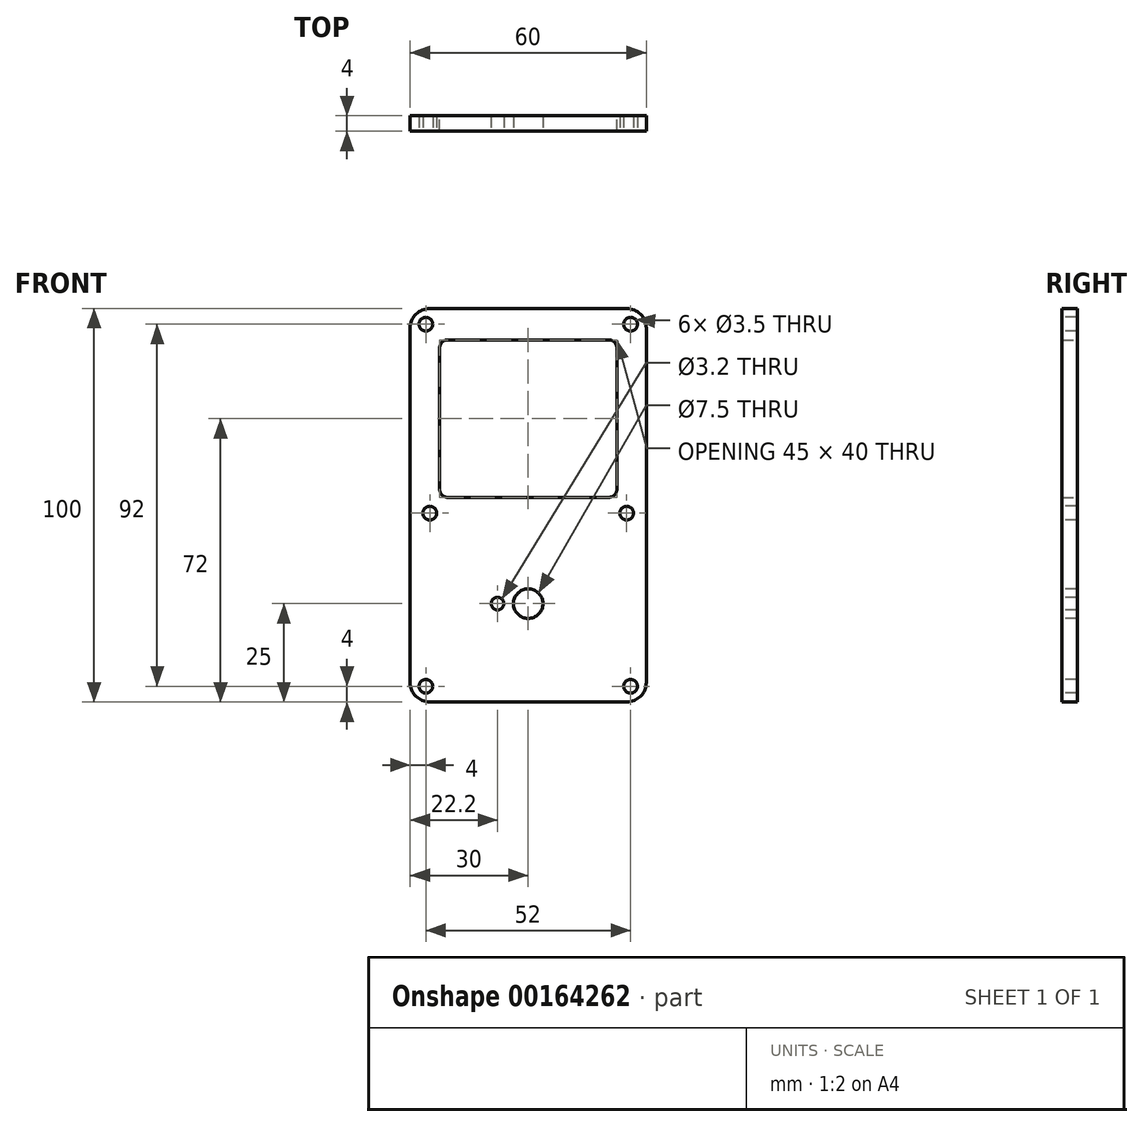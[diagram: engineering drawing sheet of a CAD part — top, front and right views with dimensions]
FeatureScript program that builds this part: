
annotation { "Feature Type Name" : "Feature", "Feature Type Description" : "" }
export const myFeature = defineFeature(function(context is Context, id is Id, definition is map)
    precondition{}
    {
        {
            var Q0;
            Q0=qCreatedBy(makeId("Front.planeOp"),FACE);
            var sketch = newSketch(context, id + "F0", { "sketchPlane" : qUnion([Q0])});
            skLineSegment(sketch, "E0.bottom", {"start": v(-30, 50) * mm, "end": v(30, 50) * mm});
            skLineSegment(sketch, "E0.top", {"start": v(-30, -50) * mm, "end": v(30, -50) * mm});
            skLineSegment(sketch, "E0.left", {"start": v(-30, 50) * mm, "end": v(-30, -50) * mm});
            skLineSegment(sketch, "E0.right", {"start": v(30, 50) * mm, "end": v(30, -50) * mm});
            skPoint(sketch, "E0.middle", {"position": v(0, 0) * mm});
            skLineSegment(sketch, "E1.bottom", {"start": v(-22.5, 42) * mm, "end": v(22.5, 42) * mm});
            skLineSegment(sketch, "E1.top", {"start": v(-22.5, 2) * mm, "end": v(22.5, 2) * mm});
            skLineSegment(sketch, "E1.left", {"start": v(-22.5, 42) * mm, "end": v(-22.5, 2) * mm});
            skLineSegment(sketch, "E1.right", {"start": v(22.5, 42) * mm, "end": v(22.5, 2) * mm});
            skSolve(sketch);
        }
        {
            var Q0;
            Q0 = qSketchRegion(id + "F0", true);
            extrude(context, id + "F1", {"entities" : qUnion([Q0]), "depth" : 4 * mm});
        }
        {
            var Q0;
            Q0=makeQuery(id+"F1.opExtrude","CAP_FACE",FACE,{"disambiguationData":[OSD([sQuery(id+"F0.wireOp",EDGE,"E0.bottom"),sQuery(id+"F0.wireOp",EDGE,"E0.top"),sQuery(id+"F0.wireOp",EDGE,"E0.left"),sQuery(id+"F0.wireOp",EDGE,"E0.right"),sQuery(id+"F0.wireOp",EDGE,"E1.bottom"),sQuery(id+"F0.wireOp",EDGE,"E1.top"),sQuery(id+"F0.wireOp",EDGE,"E1.left"),sQuery(id+"F0.wireOp",EDGE,"E1.right")])],"isStart":false});
            var sketch = newSketch(context, id + "F2", { "sketchPlane" : qUnion([Q0])});
            skLineSegment(sketch, "E2.bottom", {"start": v(-26, 46) * mm, "end": v(26, 46) * mm});
            skLineSegment(sketch, "E2.top", {"start": v(-26, -46) * mm, "end": v(26, -46) * mm});
            skLineSegment(sketch, "E2.left", {"start": v(-26, 46) * mm, "end": v(-26, -46) * mm});
            skLineSegment(sketch, "E2.right", {"start": v(26, 46) * mm, "end": v(26, -46) * mm});
            skPoint(sketch, "E2.middle", {"position": v(0, 0) * mm});
            skPoint(sketch, "E3", {"position": v(0, -25) * mm});
            skSolve(sketch);
        }
        {
            var Q0;
            Q0=sQuery(id+"F2.wireOp",VERTEX,"E2.left.start");
            var Q1;
            Q1=sQuery(id+"F2.wireOp",VERTEX,"E2.right.start");
            var Q2;
            Q2=sQuery(id+"F2.wireOp",VERTEX,"c73e0ecb-fc85-44dc-a880-6b6466e35b10");
            var Q3;
            Q3=sQuery(id+"F2.wireOp",VERTEX,"E2.top.end");
            var Q4;
            Q4=sQuery(id+"F2.wireOp",VERTEX,"E2.left.end");
            var Q5;
            Q5=sQuery(id+"F2.wireOp",VERTEX,"a1096d60-7892-4570-80c7-3819a983ac6c");
            var Q6;
            Q6=makeQuery(id+"F1.opExtrude","SWEPT_BODY",BODY,{"disambiguationData":[OSD([sQuery(id+"F0.wireOp",EDGE,"E0.bottom"),sQuery(id+"F0.wireOp",EDGE,"E0.top"),sQuery(id+"F0.wireOp",EDGE,"E0.left"),sQuery(id+"F0.wireOp",EDGE,"E0.right"),sQuery(id+"F0.wireOp",EDGE,"E1.bottom"),sQuery(id+"F0.wireOp",EDGE,"E1.top"),sQuery(id+"F0.wireOp",EDGE,"E1.left"),sQuery(id+"F0.wireOp",EDGE,"E1.right")])]});
            hole(context, id + "F3", {"style" : HoleStyle.SIMPLE, "endStyle" : HoleEndStyle.BLIND, "holeDiameter" : 3.5 * mm, "holeDepth" : 25 * mm, "startFromSketch" : true, "locations" : qUnion([Q0, Q1, Q2, Q3, Q4, Q5]), "scope" : qUnion([Q6])});
        }
        {
            var Q0;
            Q0=makeQuery(id+"F1.opExtrude","CAP_FACE",FACE,{"disambiguationData":[OSD([sQuery(id+"F0.wireOp",EDGE,"E0.bottom"),sQuery(id+"F0.wireOp",EDGE,"E0.top"),sQuery(id+"F0.wireOp",EDGE,"E0.left"),sQuery(id+"F0.wireOp",EDGE,"E0.right"),sQuery(id+"F0.wireOp",EDGE,"E1.bottom"),sQuery(id+"F0.wireOp",EDGE,"E1.top"),sQuery(id+"F0.wireOp",EDGE,"E1.left"),sQuery(id+"F0.wireOp",EDGE,"E1.right")])],"isStart":false});
            var sketch = newSketch(context, id + "F4", { "sketchPlane" : qUnion([Q0])});
            skPoint(sketch, "E4", {"position": v(0, -25) * mm});
            skCircle(sketch, "E5", {"center": v(0, -25) * mm, "radius": 3.75 * mm});
            skPoint(sketch, "E6", {"position": v(-7.8, -25) * mm});
            skCircle(sketch, "E7", {"center": v(-7.8, -25) * mm, "radius": 1.6 * mm});
            skSolve(sketch);
        }
        {
            var Q0;
            Q0=makeQuery(id+"F1.opExtrude","SWEPT_EDGE",EDGE,{"disambiguationData":[OSD([sQuery(id+"F0.wireOp",EDGE,"E0.bottom"),sQuery(id+"F0.wireOp",EDGE,"E0.left")])]});
            var Q1;
            Q1=makeQuery(id+"F1.opExtrude","SWEPT_EDGE",EDGE,{"disambiguationData":[OSD([sQuery(id+"F0.wireOp",EDGE,"E0.top"),sQuery(id+"F0.wireOp",EDGE,"E0.left")])]});
            var Q2;
            Q2=makeQuery(id+"F1.opExtrude","SWEPT_EDGE",EDGE,{"disambiguationData":[OSD([sQuery(id+"F0.wireOp",EDGE,"E0.top"),sQuery(id+"F0.wireOp",EDGE,"E0.right")])]});
            var Q3;
            Q3=makeQuery(id+"F1.opExtrude","SWEPT_EDGE",EDGE,{"disambiguationData":[OSD([sQuery(id+"F0.wireOp",EDGE,"E0.bottom"),sQuery(id+"F0.wireOp",EDGE,"E0.right")])]});
            fillet(context, id + "F5", {"entities" : qUnion([Q0, Q1, Q2, Q3]), "radius" : 5 * mm, "tangentPropagation" : true, "allowEdgeOverflow" : false});
        }
        {
            var Q0;
            Q0=makeQuery(id+"F1.opExtrude","SWEPT_EDGE",EDGE,{"disambiguationData":[OSD([sQuery(id+"F0.wireOp",EDGE,"E1.top"),sQuery(id+"F0.wireOp",EDGE,"E1.left")])]});
            var Q1;
            Q1=makeQuery(id+"F1.opExtrude","SWEPT_EDGE",EDGE,{"disambiguationData":[OSD([sQuery(id+"F0.wireOp",EDGE,"E1.bottom"),sQuery(id+"F0.wireOp",EDGE,"E1.left")])]});
            var Q2;
            Q2=makeQuery(id+"F1.opExtrude","SWEPT_EDGE",EDGE,{"disambiguationData":[OSD([sQuery(id+"F0.wireOp",EDGE,"E1.bottom"),sQuery(id+"F0.wireOp",EDGE,"E1.right")])]});
            var Q3;
            Q3=makeQuery(id+"F1.opExtrude","SWEPT_EDGE",EDGE,{"disambiguationData":[OSD([sQuery(id+"F0.wireOp",EDGE,"E1.top"),sQuery(id+"F0.wireOp",EDGE,"E1.right")])]});
            fillet(context, id + "F6", {"entities" : qUnion([Q0, Q1, Q2, Q3]), "radius" : 2 * mm, "tangentPropagation" : true, "allowEdgeOverflow" : false});
        }
        {
            var Q0;
            Q0=makeQuery(id+"F1.opExtrude","CAP_FACE",FACE,{"disambiguationData":[OSD([sQuery(id+"F0.wireOp",EDGE,"E0.bottom"),sQuery(id+"F0.wireOp",EDGE,"E0.top"),sQuery(id+"F0.wireOp",EDGE,"E0.left"),sQuery(id+"F0.wireOp",EDGE,"E0.right"),sQuery(id+"F0.wireOp",EDGE,"E1.bottom"),sQuery(id+"F0.wireOp",EDGE,"E1.top"),sQuery(id+"F0.wireOp",EDGE,"E1.left"),sQuery(id+"F0.wireOp",EDGE,"E1.right")])],"isStart":false});
            var sketch = newSketch(context, id + "F7", { "sketchPlane" : qUnion([Q0])});
            skPoint(sketch, "E8", {"position": v(-25, -2) * mm});
            skPoint(sketch, "E9.MirrorP", {"position": v(25, -2) * mm});
            skSolve(sketch);
        }
        {
            var Q0;
            Q0=sQuery(id+"F7.wireOp",VERTEX,"E8");
            var Q1;
            Q1=sQuery(id+"F7.wireOp",VERTEX,"E9.MirrorP");
            var Q2;
            Q2=makeQuery(id+"F1.opExtrude","SWEPT_BODY",BODY,{"disambiguationData":[OSD([sQuery(id+"F0.wireOp",EDGE,"E0.bottom"),sQuery(id+"F0.wireOp",EDGE,"E0.top"),sQuery(id+"F0.wireOp",EDGE,"E0.left"),sQuery(id+"F0.wireOp",EDGE,"E0.right"),sQuery(id+"F0.wireOp",EDGE,"E1.bottom"),sQuery(id+"F0.wireOp",EDGE,"E1.top"),sQuery(id+"F0.wireOp",EDGE,"E1.left"),sQuery(id+"F0.wireOp",EDGE,"E1.right")])]});
            hole(context, id + "F8", {"style" : HoleStyle.SIMPLE, "endStyle" : HoleEndStyle.BLIND, "holeDiameter" : 3.5 * mm, "holeDepth" : 25 * mm, "startFromSketch" : true, "locations" : qUnion([Q0, Q1]), "scope" : qUnion([Q2])});
        }
        {
            var Q0;
            Q0 = qSketchRegion(id + "F4", true);
            extrude(context, id + "F9", {"entities" : qUnion([Q0]), "operationType" : NewBodyOperationType.REMOVE, "oppositeDirection" : true, "depth" : 25 * mm});
        }
        {
            var Q0;
            Q0 = qSketchRegion(id + "F4", true);
            extrude(context, id + "F10", {"entities" : qUnion([Q0]), "operationType" : NewBodyOperationType.REMOVE, "oppositeDirection" : true, "depth" : 25 * mm});
        }
    });
